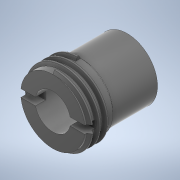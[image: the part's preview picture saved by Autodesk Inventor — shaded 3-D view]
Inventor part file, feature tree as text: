
AUTODESK INVENTOR PART (.ipt)
format: ipt  version: 2020 (Build 240168000, 168)  size: 298,496 bytes
history: native  units: mm
features: sketch x5, extrude x3, sweep x1, chamfer x1, fillet x1, projected_geometry x1, other x1
ambient origin geometry x8: Origin, YZ Plane, XZ Plane, XY Plane, X Axis, Y Axis, Z Axis, Center Point
bodies: Solid1 (feature_tree)
feature tree (13):
  extrude  "Extrusion1"  Depth=12.7mm
  extrude  "Extrusion2"  Depth=5.5mm
  sweep  "Sweep1"
  extrude  "Extrusion3"  Depth=0.5mm
  chamfer  "Chamfer1"  Distance=0.45mm
  fillet  "Fillet1"  [1 undecoded]
  sketch  "Sketch1"  dims[d0=12.7mm d1=7.0mm]
  sketch  "Sketch2"  dims[d2=5.5mm d3=0.0mm d4=12.0mm]
  sketch  "Sketch3"  dims[d5=9.2mm d6=0.0mm d10=1.5mm d11=30.0mm d12=12.7mm d13=0.0mm]
  projected_geometry  "Projected Loop1"
  sketch  "3D Sketch1"
  other  "Helical Curve1"
  sketch  "Sketch4"  dims[d14=1.0mm d15=0.2mm d16=0.45mm d17=0.0mm d18=0.0mm d19=20.0mm d20=1.5mm d21=2.0mm d22=0.0mm d23=0.35mm d24=2.0mm d25=45.0deg d26=0.5mm]
note: 1 required parameter value undecoded (feature->parameter linkage not recoverable at this tier; creation-order binding heuristic only, values carry confidence <= 0.55)
